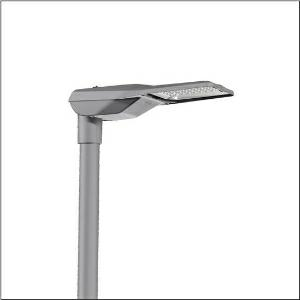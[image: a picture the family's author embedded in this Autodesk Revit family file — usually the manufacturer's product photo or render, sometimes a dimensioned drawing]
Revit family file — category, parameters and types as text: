
# Revit family: streetlight_sl_21_mini___stw1_0a_5xe2e33s08hb_4f98
name_source: partatom
category: Lighting Fixtures
units: mm (PartAtom-declared; Revit-internal decimal feet)

## family parameters
Cut with Voids When Loaded = No
Host = Face
Light Source = No
Part Type = Normal
Room Calculation Point = No
Round Connector Dimension = Use Diameter
Shared = No

## types (1)
- --- (1 x LED, 9040 lm, 66 W, 3000K)
    Apparent Load = 66 VA
    CIE Flux Codes = 38 75 98 100 100
    Color Rendering = 70
    Color Temperature = 3000K
    Default Elevation = 1800 mm
    Description = Streetlight SL 21 mini, mast luminaire, primary light control with lens, of PMMA, primary optical cover: cover, of toughened safety glass, transparent, light distribution: STW1.0a, light emission: direct distribution, primary light characteristic: asymmetric, installation type: side-entry, post-top, LED, High Power LED, rated luminous flux: 9.040lm, luminous efficacy: 137lm/W, light colour: 730, colour temperature: 3000K, control gear: D4i, control: overheat protection, constant luminous flux control, time-dependent luminous flux control, flexible luminous flux parameterisation, pre-setting: logarithmic dimming characteristic, mains connection: 220..240V, AC, 50/60Hz, start of lifetime: 66W, end of service life: 69W, reduction: 30W, luminaire housing, of diecast aluminium, powder-coated, SITECO metallic grey (DB 702S), corrosivity category C5 high according to DIN EN ISO 12944, please order mast flange separately, inclination adjustable: 0°, 5°, 10°, 15°, sealing non-destructively replaceable, multi-level sealing system, length: 628mm, width: 235mm, height: 110mm, mast flange for spigot size: 42mm (side-entry): 5XC10008XM4, 60/48mm (side-entry/post-top): 5XC10108XM2, 76/60mm (side-entry/post-top): 5XC10108XM1, mounting height: 4..8m, Smart Interface above, protection rating (complete): IP66, insulation class (complete): insulation class II (safety insulation), certification: CE, ENEC, ENEC+, VDE, impact resistance: IK10, permissible operating ambient temperature for outdoor applications: -40..+50°C, standard-compliant lighting for roads and squares, packaging unit: 1 piece

Light Distribution: STW1.0a
    Height = 110 mm
    Lamp = 1 x LED
    Lamp Light Flux = 9040 lm
    Lamp Power = 66 W
    Lamp count = 1
    Length = 625 mm
    Luminous efficacy = 137 lm/W
    Manufacturer = Siteco
    ModVariant = No
    Model = 5XE2E33S08HB
    Number of Poles = 1
    OnlyDefault = Yes
    Power Factor = 1
    Product Name = Streetlight SL 21 mini | STW1.0a
    Product group = mast luminaire | pylon top
    ProductGroupID = 6100
    Protection Class = Protection class II
    Protection Degree = IP 66
    RLX_Detail_Level = 1
    RLX_Emergency_Light_Flux = 0 lm
    RLX_Emergency_Type = 0
    RLX_Emergency_Type_DB = No
    RlxData = <blob elided: 26165 chars, md5=5ecd8620>
    Socket = socket
    Standby Power = 0 W
    System Light Flux = 9040 lm
    System Power = 66 W
    Type Comments = factory setting: luminous flux: 100 % | dim-lin: 254 | 670 mA
    Type Image = l_1003515.jpg
    URL = http://relux.com
    VarID = @adj_184835
    Voltage = 0 V
    Weight = 0.00 kg
    Width = 234 mm

## geometry (parser evidence)
native form markers: Blend x4, Sweep x12
no freeform markers — native parametric forms only
